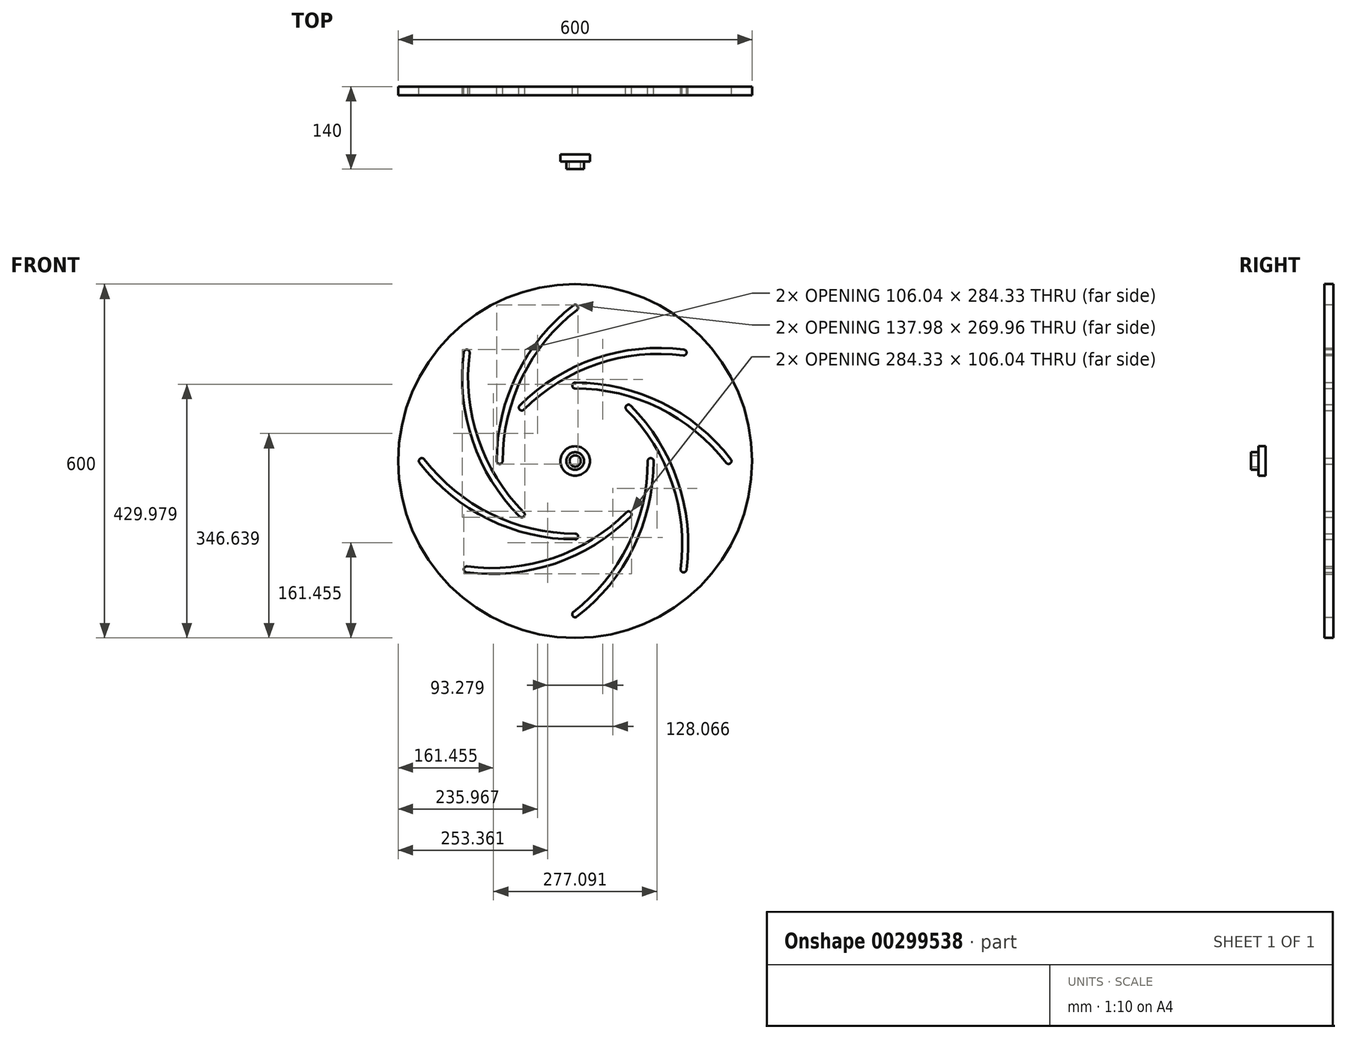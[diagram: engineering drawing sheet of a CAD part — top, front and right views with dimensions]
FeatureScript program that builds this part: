
annotation { "Feature Type Name" : "Feature", "Feature Type Description" : "" }
export const myFeature = defineFeature(function(context is Context, id is Id, definition is map)
    precondition{}
    {
        {
            var Q0;
            Q0=qCreatedBy(makeId("Front.planeOp"),FACE);
            var sketch = newSketch(context, id + "F0", { "sketchPlane" : qUnion([Q0])});
            skCircle(sketch, "E0", {"center": v(0, 0) * mm, "radius": 300 * mm});
            skCircle(sketch, "E1", {"center": v(0, 0) * mm, "radius": 260 * mm, "construction": true});
            skLineSegment(sketch, "E2", {"start": v(0, 0) * mm, "end": v(0, 260) * mm, "construction": true});
            skLineSegment(sketch, "E3", {"start": v(0, 0) * mm, "end": v(183.85, 183.85) * mm, "construction": true});
            skLineSegment(sketch, "E4", {"start": v(0, 0) * mm, "end": v(260, 0) * mm, "construction": true});
            skLineSegment(sketch, "E5", {"start": v(0, 0) * mm, "end": v(183.85, -183.85) * mm, "construction": true});
            skLineSegment(sketch, "E6", {"start": v(0, 0) * mm, "end": v(0, -260) * mm, "construction": true});
            skLineSegment(sketch, "E7", {"start": v(0, 0) * mm, "end": v(-183.85, -183.85) * mm, "construction": true});
            skLineSegment(sketch, "E8", {"start": v(0, 0) * mm, "end": v(-260, 0) * mm, "construction": true});
            skLineSegment(sketch, "E9", {"start": v(0, 0) * mm, "end": v(-183.85, 183.85) * mm, "construction": true});
            skCircle(sketch, "E10", {"center": v(0, 0) * mm, "radius": 200 * mm, "construction": true});
            skArc(sketch, "E11", {"start": v(0, 260) * mm, "mid": v(-94.28, 144.9) * mm, "end": v(-128.02, 0) * mm, "construction": true});
            skArc(sketch, "E12", {"start": v(183.85, 183.85) * mm, "mid": v(35.8, 169.13) * mm, "end": v(-90.53, 90.53) * mm, "construction": true});
            skArc(sketch, "E13.0.startCap", {"start": v(-3.05, 263.96) * mm, "mid": v(3.96, 263.05) * mm, "end": v(3.05, 256.04) * mm});
            skArc(sketch, "E13.0.endCap", {"start": v(-123.02, 0) * mm, "mid": v(-128.02, -5) * mm, "end": v(-133.02, 0) * mm});
            skArc(sketch, "E13.0.left", {"start": v(3.05, 256.04) * mm, "mid": v(-89.8, 142.7) * mm, "end": v(-123.02, 0) * mm});
            skArc(sketch, "E13.0.right", {"start": v(-3.05, 263.96) * mm, "mid": v(-98.77, 147.11) * mm, "end": v(-133.02, 0) * mm});
            skArc(sketch, "E13.1.startCap", {"start": v(184.5, 188.8) * mm, "mid": v(188.8, 183.2) * mm, "end": v(183.2, 178.89) * mm});
            skArc(sketch, "E13.1.endCap", {"start": v(-87, 87) * mm, "mid": v(-94.06, 87) * mm, "end": v(-94.06, 94.06) * mm});
            skArc(sketch, "E13.1.left", {"start": v(183.2, 178.89) * mm, "mid": v(37.4, 164.4) * mm, "end": v(-87, 87) * mm});
            skArc(sketch, "E13.1.right", {"start": v(184.5, 188.8) * mm, "mid": v(34.19, 173.87) * mm, "end": v(-94.06, 94.06) * mm});
            skArc(sketch, "E14.1.0", {"start": v(-263.96, -3.05) * mm, "mid": v(-147.11, -98.77) * mm, "end": v(0, -133.02) * mm});
            skArc(sketch, "E14.1.1", {"start": v(-256.04, 3.05) * mm, "mid": v(-142.7, -89.8) * mm, "end": v(0, -123.02) * mm});
            skArc(sketch, "E14.1.2", {"start": v(0, -123.02) * mm, "mid": v(5, -128.02) * mm, "end": v(0, -133.02) * mm});
            skArc(sketch, "E14.1.3", {"start": v(-188.8, 184.5) * mm, "mid": v(-173.87, 34.19) * mm, "end": v(-94.06, -94.06) * mm});
            skArc(sketch, "E14.1.4", {"start": v(-178.89, 183.2) * mm, "mid": v(-164.4, 37.4) * mm, "end": v(-87, -87) * mm});
            skArc(sketch, "E14.1.5", {"start": v(-87, -87) * mm, "mid": v(-87, -94.06) * mm, "end": v(-94.06, -94.06) * mm});
            skArc(sketch, "E14.1.6", {"start": v(-263.96, -3.05) * mm, "mid": v(-263.05, 3.96) * mm, "end": v(-256.04, 3.05) * mm});
            skArc(sketch, "E14.1.7", {"start": v(-188.8, 184.5) * mm, "mid": v(-183.2, 188.8) * mm, "end": v(-178.89, 183.2) * mm});
            skArc(sketch, "E14.2.0", {"start": v(3.05, -263.96) * mm, "mid": v(98.77, -147.11) * mm, "end": v(133.02, 0) * mm});
            skArc(sketch, "E14.2.1", {"start": v(-3.05, -256.04) * mm, "mid": v(89.8, -142.7) * mm, "end": v(123.02, 0) * mm});
            skArc(sketch, "E14.2.2", {"start": v(123.02, 0) * mm, "mid": v(128.02, 5) * mm, "end": v(133.02, 0) * mm});
            skArc(sketch, "E14.2.3", {"start": v(-184.5, -188.8) * mm, "mid": v(-34.19, -173.87) * mm, "end": v(94.06, -94.06) * mm});
            skArc(sketch, "E14.2.4", {"start": v(-183.2, -178.89) * mm, "mid": v(-37.4, -164.4) * mm, "end": v(87, -87) * mm});
            skArc(sketch, "E14.2.5", {"start": v(87, -87) * mm, "mid": v(94.06, -87) * mm, "end": v(94.06, -94.06) * mm});
            skArc(sketch, "E14.2.6", {"start": v(3.05, -263.96) * mm, "mid": v(-3.96, -263.05) * mm, "end": v(-3.05, -256.04) * mm});
            skArc(sketch, "E14.2.7", {"start": v(-184.5, -188.8) * mm, "mid": v(-188.8, -183.2) * mm, "end": v(-183.2, -178.89) * mm});
            skArc(sketch, "E14.3.0", {"start": v(263.96, 3.05) * mm, "mid": v(147.11, 98.77) * mm, "end": v(0, 133.02) * mm});
            skArc(sketch, "E14.3.1", {"start": v(256.04, -3.05) * mm, "mid": v(142.7, 89.8) * mm, "end": v(0, 123.02) * mm});
            skArc(sketch, "E14.3.2", {"start": v(0, 123.02) * mm, "mid": v(-5, 128.02) * mm, "end": v(0, 133.02) * mm});
            skArc(sketch, "E14.3.3", {"start": v(188.8, -184.5) * mm, "mid": v(173.87, -34.19) * mm, "end": v(94.06, 94.06) * mm});
            skArc(sketch, "E14.3.4", {"start": v(178.89, -183.2) * mm, "mid": v(164.4, -37.4) * mm, "end": v(87, 87) * mm});
            skArc(sketch, "E14.3.5", {"start": v(87, 87) * mm, "mid": v(87, 94.06) * mm, "end": v(94.06, 94.06) * mm});
            skArc(sketch, "E14.3.6", {"start": v(263.96, 3.05) * mm, "mid": v(263.05, -3.96) * mm, "end": v(256.04, -3.05) * mm});
            skArc(sketch, "E14.3.7", {"start": v(188.8, -184.5) * mm, "mid": v(183.2, -188.8) * mm, "end": v(178.89, -183.2) * mm});
            skSolve(sketch);
        }
        {
            var Q0;
            Q0=makeQuery(id+"F0.imprint","IMPRINT",FACE,{"disambiguationData":[TD([[makeQuery(id+"F0.imprint","IMPRINT",EDGE,{"derivedFrom":sQuery(id+"F0.wireOp",EDGE,"E0")}),1.0]])]});
            extrude(context, id + "F1", {"entities" : qUnion([Q0]), "depth" : 15 * mm});
        }
        {
            var Q0;
            Q0=makeQuery(id+"F1.opExtrude","CAP_FACE",FACE,{"disambiguationData":[OSD([sQuery(id+"F0.wireOp",EDGE,"E0"),sQuery(id+"F0.wireOp",EDGE,"190217d5-cf17-48d6-b099-e25173193376.0.startCap"),sQuery(id+"F0.wireOp",EDGE,"190217d5-cf17-48d6-b099-e25173193376.0.endCap"),sQuery(id+"F0.wireOp",EDGE,"190217d5-cf17-48d6-b099-e25173193376.0.left"),sQuery(id+"F0.wireOp",EDGE,"190217d5-cf17-48d6-b099-e25173193376.0.right"),sQuery(id+"F0.wireOp",EDGE,"190217d5-cf17-48d6-b099-e25173193376.1.startCap"),sQuery(id+"F0.wireOp",EDGE,"190217d5-cf17-48d6-b099-e25173193376.1.endCap"),sQuery(id+"F0.wireOp",EDGE,"190217d5-cf17-48d6-b099-e25173193376.1.left"),sQuery(id+"F0.wireOp",EDGE,"190217d5-cf17-48d6-b099-e25173193376.1.right"),sQuery(id+"F0.wireOp",EDGE,"6f756a5c-930b-4008-9d06-f06ca9c0c48a.1.0"),sQuery(id+"F0.wireOp",EDGE,"6f756a5c-930b-4008-9d06-f06ca9c0c48a.1.1"),sQuery(id+"F0.wireOp",EDGE,"6f756a5c-930b-4008-9d06-f06ca9c0c48a.1.2"),sQuery(id+"F0.wireOp",EDGE,"6f756a5c-930b-4008-9d06-f06ca9c0c48a.1.3"),sQuery(id+"F0.wireOp",EDGE,"6f756a5c-930b-4008-9d06-f06ca9c0c48a.1.4"),sQuery(id+"F0.wireOp",EDGE,"6f756a5c-930b-4008-9d06-f06ca9c0c48a.1.5"),sQuery(id+"F0.wireOp",EDGE,"6f756a5c-930b-4008-9d06-f06ca9c0c48a.1.6"),sQuery(id+"F0.wireOp",EDGE,"6f756a5c-930b-4008-9d06-f06ca9c0c48a.1.7"),sQuery(id+"F0.wireOp",EDGE,"6f756a5c-930b-4008-9d06-f06ca9c0c48a.2.0"),sQuery(id+"F0.wireOp",EDGE,"6f756a5c-930b-4008-9d06-f06ca9c0c48a.2.1"),sQuery(id+"F0.wireOp",EDGE,"6f756a5c-930b-4008-9d06-f06ca9c0c48a.2.2"),sQuery(id+"F0.wireOp",EDGE,"6f756a5c-930b-4008-9d06-f06ca9c0c48a.2.3"),sQuery(id+"F0.wireOp",EDGE,"6f756a5c-930b-4008-9d06-f06ca9c0c48a.2.4"),sQuery(id+"F0.wireOp",EDGE,"6f756a5c-930b-4008-9d06-f06ca9c0c48a.2.5"),sQuery(id+"F0.wireOp",EDGE,"6f756a5c-930b-4008-9d06-f06ca9c0c48a.2.6"),sQuery(id+"F0.wireOp",EDGE,"6f756a5c-930b-4008-9d06-f06ca9c0c48a.2.7"),sQuery(id+"F0.wireOp",EDGE,"6f756a5c-930b-4008-9d06-f06ca9c0c48a.3.0"),sQuery(id+"F0.wireOp",EDGE,"6f756a5c-930b-4008-9d06-f06ca9c0c48a.3.1"),sQuery(id+"F0.wireOp",EDGE,"6f756a5c-930b-4008-9d06-f06ca9c0c48a.3.2"),sQuery(id+"F0.wireOp",EDGE,"6f756a5c-930b-4008-9d06-f06ca9c0c48a.3.3"),sQuery(id+"F0.wireOp",EDGE,"6f756a5c-930b-4008-9d06-f06ca9c0c48a.3.4"),sQuery(id+"F0.wireOp",EDGE,"6f756a5c-930b-4008-9d06-f06ca9c0c48a.3.5"),sQuery(id+"F0.wireOp",EDGE,"6f756a5c-930b-4008-9d06-f06ca9c0c48a.3.6"),sQuery(id+"F0.wireOp",EDGE,"6f756a5c-930b-4008-9d06-f06ca9c0c48a.3.7"),sQuery(id+"F0.wireOp",EDGE,"aRzY6Wkb-WaI1-5VvA-zSoj-qroDh9XZPMvn")])],"isStart":false});
            cPlane(context, id + "F2", {"entities" : qUnion([Q0]), "cplaneType" : CPlaneType.OFFSET, "offset" : 100 * mm, "width" : 150 * mm, "height" : 150 * mm});
        }
        {
            var Q0;
            Q0=qCreatedBy(id+"F2.planeOp",FACE);
            var sketch = newSketch(context, id + "F3", { "sketchPlane" : qUnion([Q0])});
            skCircle(sketch, "E15", {"center": v(0, 0) * mm, "radius": 25 * mm});
            skCircle(sketch, "E16", {"center": v(0, 0) * mm, "radius": 15 * mm});
            skCircle(sketch, "E17", {"center": v(0, 0) * mm, "radius": 9.53 * mm});
            skSolve(sketch);
        }
        {
            var Q0;
            Q0=makeQuery(id+"F3.imprint","IMPRINT",FACE,{"disambiguationData":[TD([[makeQuery(id+"F3.imprint","IMPRINT",EDGE,{"derivedFrom":sQuery(id+"F3.wireOp",EDGE,"E16")}),1.0]])]});
            extrude(context, id + "F4", {"entities" : qUnion([Q0]), "depth" : 25 * mm});
        }
        {
            var Q0;
            Q0=makeQuery(id+"F3.imprint","IMPRINT",FACE,{"disambiguationData":[TD([[makeQuery(id+"F3.imprint","IMPRINT",EDGE,{"derivedFrom":sQuery(id+"F3.wireOp",EDGE,"E15")}),1.0]])]});
            extrude(context, id + "F5", {"entities" : qUnion([Q0]), "operationType" : NewBodyOperationType.ADD, "depth" : 12 * mm});
        }
    });
